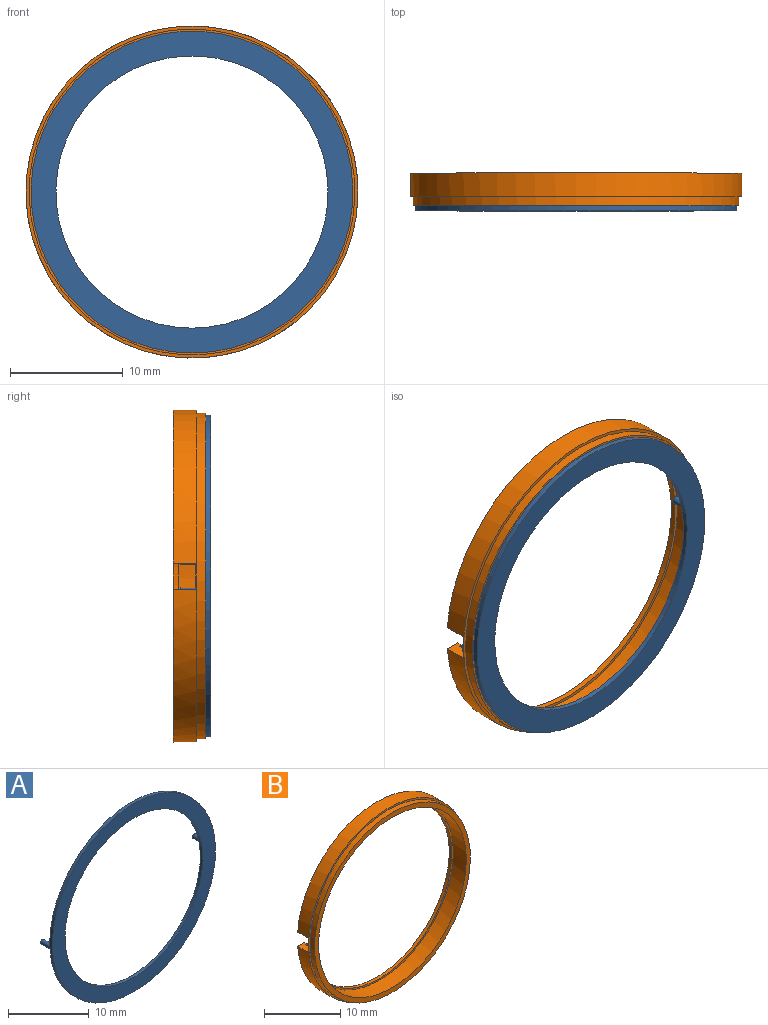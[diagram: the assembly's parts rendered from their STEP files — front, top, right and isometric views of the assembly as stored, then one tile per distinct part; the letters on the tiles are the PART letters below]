
ASSEMBLY  parts=2 mates=1
PART A: 8 faces, bbox 28.5x2.7x28.5 mm
  f0: cylinder r=12.05mm len=24.1mm, axis (0,1,0), area 34.1mm2, adj f2,f3
  f1: cylinder r=14.25mm len=28.5mm, axis (0,1,0), area 40.3mm2, adj f2,f3
  f2: plane 28.5x28.5mm, normal (0,-1,0), area 181.8mm2, adj f0,f1
  f3: plane 28.5x28.5mm, normal (0,1,0), area 181.1mm2, adj f0,f1,f4,f6
  f4: cylinder r=0.33mm len=2.25mm, axis (0,-1,0), area 4.7mm2, adj f3,f5
  f5: plane 0.66x0.66mm, normal (0,1,0), area 0.3mm2, adj f4
  f6: cylinder r=0.33mm len=2.25mm, axis (0,-1,0), area 4.7mm2, adj f3,f7
  f7: plane 0.66x0.66mm, normal (0,1,0), area 0.3mm2, adj f6
PART B: 11 faces, bbox 29.4x2.9x29.4 mm
  f0: plane 27.35x27.3mm, normal (0,-1,0), area 22.6mm2, adj f1,f4,f8,f9
  f1: cylinder r=13.4mm len=26.8mm, axis (0,1,0), area 39.3mm2, adj f0,f2,f8,f9
  f2: plane 29.4x29.36mm, normal (0,1,0), area 111.8mm2, adj f1,f3,f8,f9
  f3: cylinder r=14.7mm len=29.4mm, axis (0,1,0), area 186.6mm2, adj f2,f5,f8,f9,f10
  f4: cylinder r=13.67mm len=27.35mm, axis (0,1,0), area 202.7mm2, adj f0,f7,f8,f9,f10
  f5: plane 29.4x29.4mm, normal (0,-1,0), area 25.3mm2, adj f3,f6
  f6: cylinder r=14.42mm len=28.85mm, axis (0,1,0), area 73.4mm2, adj f5,f7
  f7: plane 28.85x28.85mm, normal (0,-1,0), area 66.2mm2, adj f4,f6
  f8: plane 2x1.3mm, normal (0,0,-1), area 2.2mm2, adj f0,f1,f2,f3,f4,f10
  f9: plane 2x1.3mm, normal (0,0,1), area 2.2mm2, adj f0,f1,f2,f3,f4,f10
  f10: plane 2.3x1.08mm, normal (0,1,0), area 2.4mm2, adj f3,f4,f8,f9
PLACE A t=(9.13,33.69,-5.34)mm
PLACE B t=(-30.56,35.13,-5.34)mm
MATE fastened B.f1 <-> A.f0  axis (0,-1,0) through (9.13,33.69,-5.34)mm
